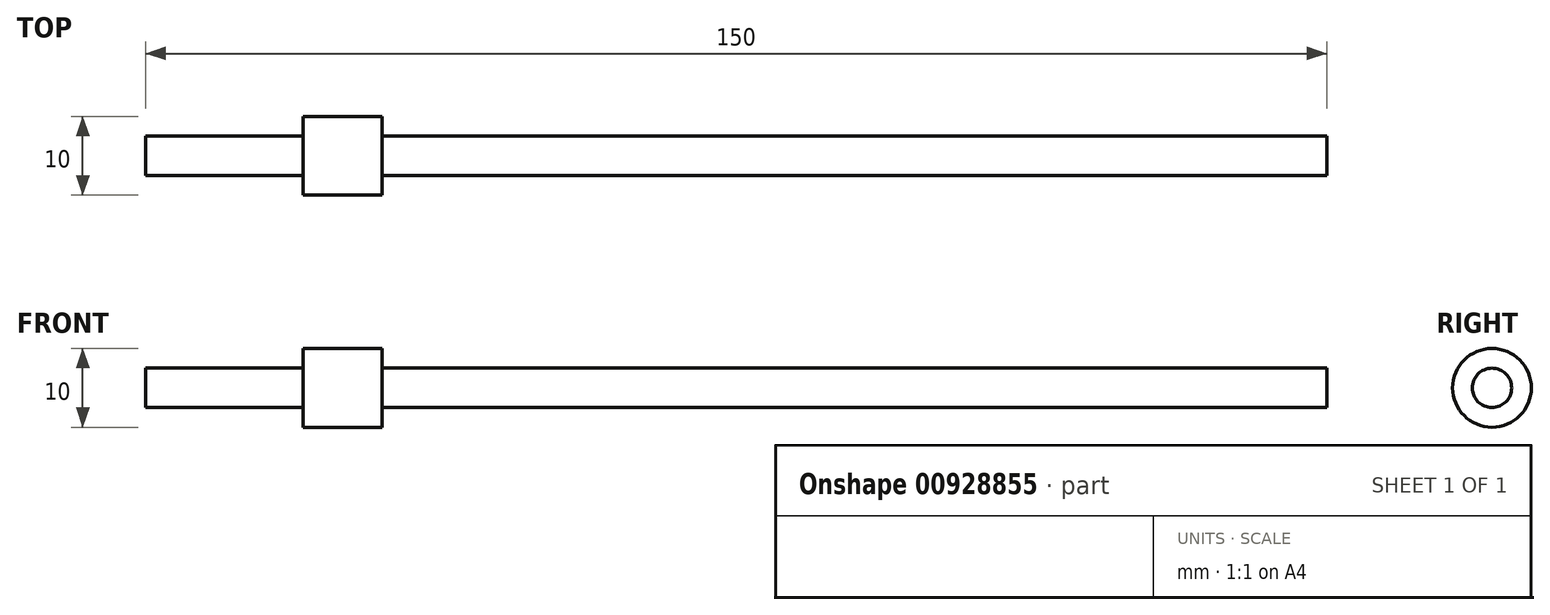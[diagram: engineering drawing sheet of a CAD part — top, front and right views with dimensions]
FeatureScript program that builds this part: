
annotation { "Feature Type Name" : "Feature", "Feature Type Description" : "" }
export const myFeature = defineFeature(function(context is Context, id is Id, definition is map)
    precondition{}
    {
        {
            var Q0;
            Q0=qCreatedBy(makeId("Front.planeOp"),FACE);
            var sketch = newSketch(context, id + "F0", { "sketchPlane" : qUnion([Q0])});
            skLineSegment(sketch, "E0", {"start": v(0, 0) * mm, "end": v(0, 2.5) * mm});
            skLineSegment(sketch, "E1", {"start": v(0, 2.5) * mm, "end": v(20, 2.5) * mm});
            skLineSegment(sketch, "E2", {"start": v(20, 2.5) * mm, "end": v(20, 5) * mm});
            skLineSegment(sketch, "E3", {"start": v(20, 5) * mm, "end": v(30, 5) * mm});
            skLineSegment(sketch, "E4", {"start": v(30, 5) * mm, "end": v(30, 2.5) * mm});
            skLineSegment(sketch, "E5", {"start": v(30, 2.5) * mm, "end": v(150, 2.5) * mm});
            skLineSegment(sketch, "E6", {"start": v(150, 2.5) * mm, "end": v(150, 0) * mm});
            skLineSegment(sketch, "E7", {"start": v(-2.24, 0) * mm, "end": v(90.14, 0) * mm, "construction": true});
            skLineSegment(sketch, "E8", {"start": v(0, 0) * mm, "end": v(150, 0) * mm});
            skSolve(sketch);
        }
        {
            var Q0;
            Q0 = qSketchRegion(id + "F0", true);
            var Q1;
            Q1=sQuery(id+"F0.wireOp",EDGE,"E7");
            revolve(context, id + "F1", {"surfaceOperationType" : NewSurfaceOperationType.NEW, "entities" : qUnion([Q0]), "axis" : qUnion([Q1]), "revolveType" : RevolveType.FULL});
        }
    });
